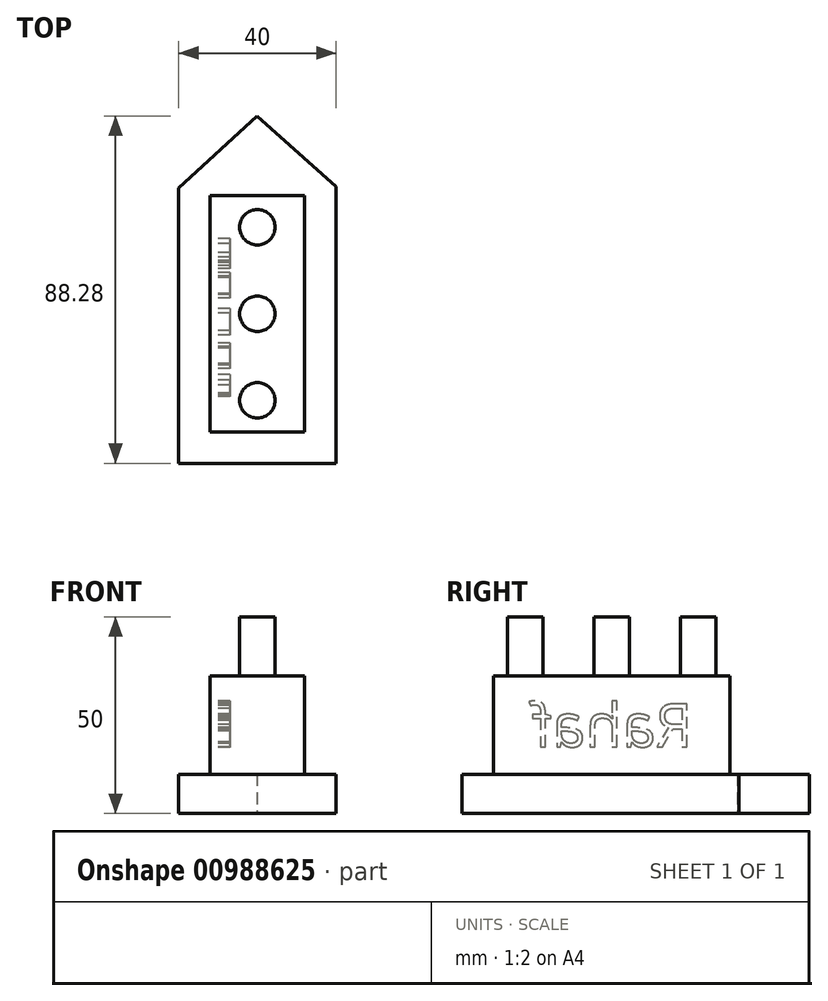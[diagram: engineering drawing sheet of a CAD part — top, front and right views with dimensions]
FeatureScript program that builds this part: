
annotation { "Feature Type Name" : "Feature", "Feature Type Description" : "" }
export const myFeature = defineFeature(function(context is Context, id is Id, definition is map)
    precondition{}
    {
        {
            var Q0;
            Q0=qCreatedBy(makeId("Top.planeOp"),FACE);
            var sketch = newSketch(context, id + "F0", { "sketchPlane" : qUnion([Q0])});
            skLineSegment(sketch, "E0", {"start": v(-20, 46.45) * mm, "end": v(-0.13, 64.73) * mm});
            skLineSegment(sketch, "E1", {"start": v(-0.13, 64.73) * mm, "end": v(20, 46.73) * mm});
            skLineSegment(sketch, "E2", {"start": v(-20, 46.45) * mm, "end": v(-20, -23.55) * mm});
            skLineSegment(sketch, "E3", {"start": v(20, -23.55) * mm, "end": v(-20, -23.55) * mm});
            skLineSegment(sketch, "E4", {"start": v(20, 46.73) * mm, "end": v(20, -23.55) * mm});
            skSolve(sketch);
        }
        {
            var Q0;
            Q0 = qSketchRegion(id + "F0", true);
            extrude(context, id + "F1", {"entities" : qUnion([Q0]), "depth" : 10 * mm, "offsetDistance" : 25 * mm});
        }
        {
            var Q0;
            Q0=makeQuery(id+"F1.opExtrude","CAP_FACE",FACE,{"disambiguationData":[OSD([sQuery(id+"F0.wireOp",EDGE,"E0"),sQuery(id+"F0.wireOp",EDGE,"E1"),sQuery(id+"F0.wireOp",EDGE,"E2"),sQuery(id+"F0.wireOp",EDGE,"E3"),sQuery(id+"F0.wireOp",EDGE,"E4")])],"isStart":false});
            var sketch = newSketch(context, id + "F2", { "sketchPlane" : qUnion([Q0])});
            skLineSegment(sketch, "E5.bottom", {"start": v(-12, 44.45) * mm, "end": v(12, 44.45) * mm});
            skLineSegment(sketch, "E5.top", {"start": v(-12, -15.55) * mm, "end": v(12, -15.55) * mm});
            skLineSegment(sketch, "E5.left", {"start": v(-12, 44.45) * mm, "end": v(-12, -15.55) * mm});
            skLineSegment(sketch, "E5.right", {"start": v(12, 44.45) * mm, "end": v(12, -15.55) * mm});
            skSolve(sketch);
        }
        {
            var Q0;
            Q0=makeQuery(id+"F2.imprint","IMPRINT",FACE,{"disambiguationData":[TD([[makeQuery(id+"F2.imprint","IMPRINT",EDGE,{"derivedFrom":sQuery(id+"F2.wireOp",EDGE,"E5.bottom")}),-1.0]])]});
            extrude(context, id + "F3", {"entities" : qUnion([Q0]), "operationType" : NewBodyOperationType.ADD, "depth" : 25 * mm, "offsetDistance" : 25 * mm});
        }
        {
            var Q0;
            Q0=makeQuery(id+"F3.opExtrude","CAP_FACE",FACE,{"disambiguationData":[OSD([sQuery(id+"F2.wireOp",EDGE,"E5.bottom"),sQuery(id+"F2.wireOp",EDGE,"E5.top"),sQuery(id+"F2.wireOp",EDGE,"E5.left"),sQuery(id+"F2.wireOp",EDGE,"E5.right")])],"isStart":false});
            var sketch = newSketch(context, id + "F4", { "sketchPlane" : qUnion([Q0])});
            skCircle(sketch, "E6", {"center": v(0, -7.55) * mm, "radius": 4.5 * mm});
            skCircle(sketch, "E7", {"center": v(0, 14.45) * mm, "radius": 4.5 * mm});
            skCircle(sketch, "E8", {"center": v(0, 36.45) * mm, "radius": 4.5 * mm});
            skSolve(sketch);
        }
        {
            var Q0;
            Q0 = qSketchRegion(id + "F4", true);
            extrude(context, id + "F5", {"entities" : qUnion([Q0]), "operationType" : NewBodyOperationType.ADD, "depth" : 15 * mm, "offsetDistance" : 25 * mm});
        }
        {
            var Q0;
            Q0=makeQuery(id+"F3.opExtrude","SWEPT_FACE",FACE,{"disambiguationData":[OSD([sQuery(id+"F2.wireOp",EDGE,"E5.left")])]});
            var sketch = newSketch(context, id + "F6", { "sketchPlane" : qUnion([Q0])});
            skText(sketch, "E9", { "text": "Rahaf", "fontName": "OpenSans-Regular.ttf"});
            const initialGuessF6  = {"E9": [-0.03509, 0.017, 1, 0, 0.011]};
            skSetInitialGuess(sketch, initialGuessF6);
            skSolve(sketch);
        }
        {
            var Q0;
            Q0 = qSketchRegion(id + "F6", true);
            extrude(context, id + "F7", {"entities" : qUnion([Q0]), "operationType" : NewBodyOperationType.REMOVE, "oppositeDirection" : true, "depth" : 5 * mm, "offsetDistance" : 25 * mm});
        }
    });
